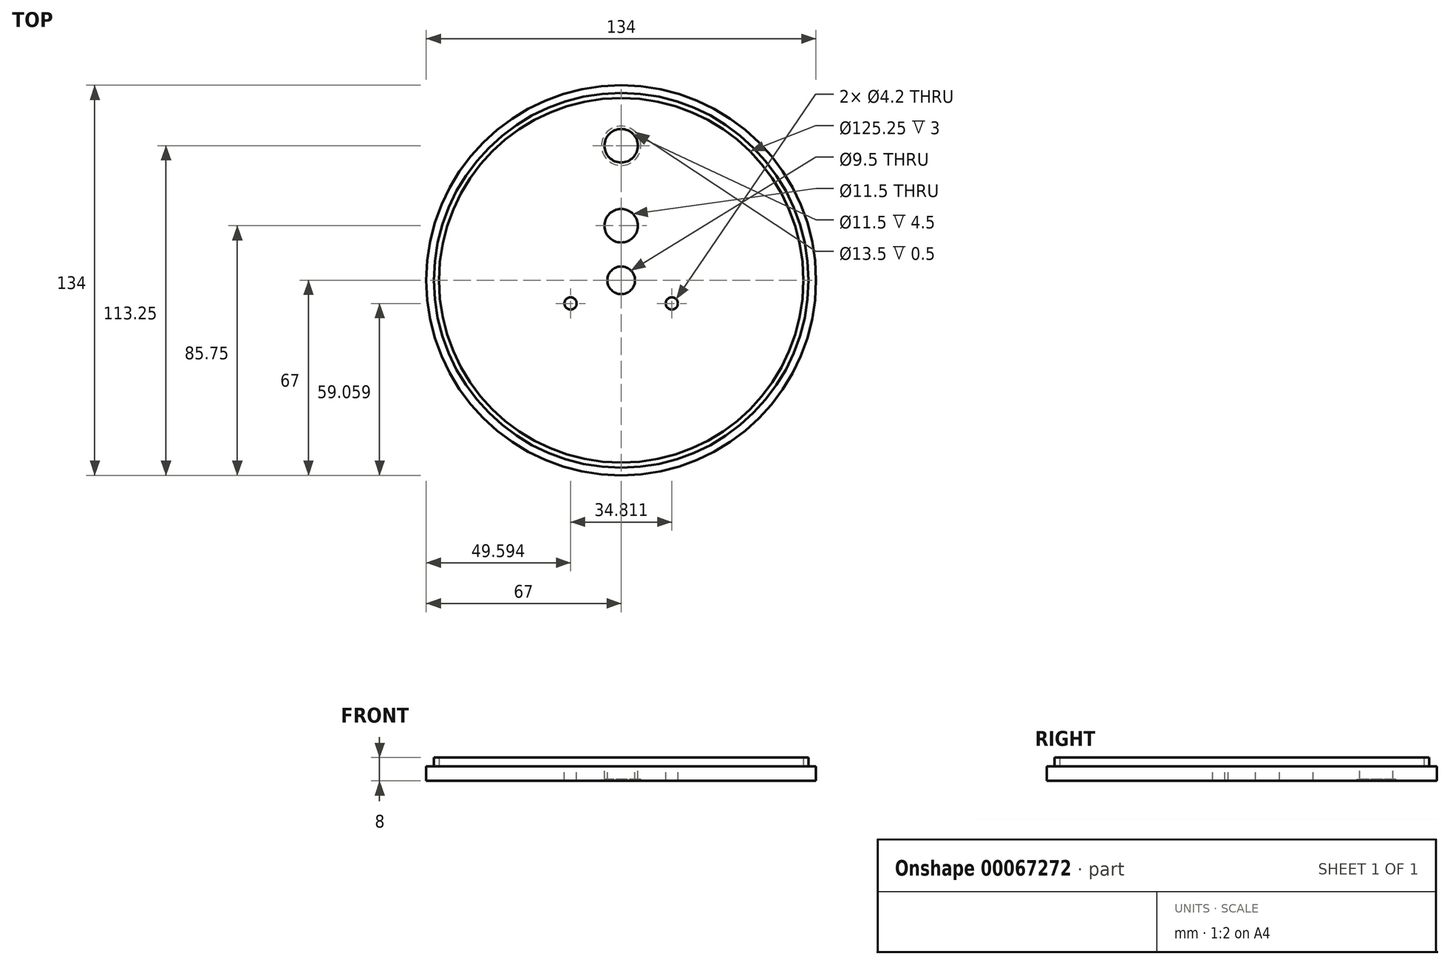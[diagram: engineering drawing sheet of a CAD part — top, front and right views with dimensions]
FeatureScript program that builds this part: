
annotation { "Feature Type Name" : "Feature", "Feature Type Description" : "" }
export const myFeature = defineFeature(function(context is Context, id is Id, definition is map)
    precondition{}
    {
        {
            var Q0;
            Q0=qCreatedBy(makeId("Top.planeOp"),FACE);
            var sketch = newSketch(context, id + "F0", { "sketchPlane" : qUnion([Q0])});
            skCircle(sketch, "E0", {"center": v(0, 0) * mm, "radius": 67 * mm});
            skSolve(sketch);
        }
        {
            var Q0;
            Q0=makeQuery(id+"F0.imprint","IMPRINT",FACE,{"disambiguationData":[TD([[makeQuery(id+"F0.imprint","IMPRINT",EDGE,{"derivedFrom":sQuery(id+"F0.wireOp",EDGE,"E0")}),1.0]])]});
            extrude(context, id + "F1", {"entities" : qUnion([Q0]), "depth" : 5 * mm});
        }
        {
            var Q0;
            Q0=makeQuery(id+"F1.opExtrude","CAP_FACE",FACE,{"disambiguationData":[OSD([sQuery(id+"F0.wireOp",EDGE,"E0")])],"isStart":false});
            var sketch = newSketch(context, id + "F2", { "sketchPlane" : qUnion([Q0])});
            skCircle(sketch, "E1", {"center": v(0, 0) * mm, "radius": 64.38 * mm});
            skSolve(sketch);
        }
        {
            var Q0;
            Q0=makeQuery(id+"F2.imprint","IMPRINT",FACE,{"disambiguationData":[TD([[makeQuery(id+"F2.imprint","IMPRINT",EDGE,{"derivedFrom":sQuery(id+"F2.wireOp",EDGE,"E1")}),1.0]])]});
            var sketch = newSketch(context, id + "F3", { "sketchPlane" : qUnion([Q0])});
            skCircle(sketch, "E2", {"center": v(0, 0) * mm, "radius": 62.62 * mm});
            skSolve(sketch);
        }
        {
            var Q0;
            Q0=makeQuery(id+"F2.imprint","IMPRINT",FACE,{"disambiguationData":[TD([[makeQuery(id+"F2.imprint","IMPRINT",EDGE,{"derivedFrom":sQuery(id+"F2.wireOp",EDGE,"E1")}),1.0]])]});
            var sketch = newSketch(context, id + "F4", { "sketchPlane" : qUnion([Q0])});
            skCircle(sketch, "E3", {"center": v(0, 0) * mm, "radius": 58.88 * mm});
            skSolve(sketch);
        }
        {
            var Q0;
            Q0=makeQuery(id+"F3.imprint","IMPRINT",FACE,{"disambiguationData":[TD([[makeQuery(id+"F3.imprint","IMPRINT",EDGE,{"derivedFrom":sQuery(id+"F3.wireOp",EDGE,"E2")}),-1.0]])]});
            var Q1;
            Q1=sQuery(id+"F2.wireOp",EDGE,"E1");
            var Q2;
            Q2=sQuery(id+"F3.wireOp",EDGE,"E2");
            extrude(context, id + "F5", {"entities" : qUnion([Q0]), "operationType" : NewBodyOperationType.ADD, "surfaceEntities" : qUnion([Q1, Q2]), "depth" : 3 * mm});
        }
        {
            var Q0;
            Q0=makeQuery(id+"F4.imprint","IMPRINT",FACE,{"disambiguationData":[TD([[makeQuery(id+"F4.imprint","IMPRINT",EDGE,{"derivedFrom":sQuery(id+"F4.wireOp",EDGE,"E3")}),1.0]])]});
            var sketch = newSketch(context, id + "F6", { "sketchPlane" : qUnion([Q0])});
            skCircle(sketch, "E4", {"center": v(0, 0) * mm, "radius": 4.75 * mm});
            skCircle(sketch, "E5", {"center": v(0, 18.75) * mm, "radius": 5.75 * mm});
            skCircle(sketch, "E6", {"center": v(0, 46.25) * mm, "radius": 5.75 * mm});
            skCircle(sketch, "E7.0", {"center": v(0, 18.75) * mm, "radius": 6.75 * mm});
            skCircle(sketch, "E8.0", {"center": v(0, 0) * mm, "radius": 63.88 * mm});
            skCircle(sketch, "E9.0", {"center": v(0, 0) * mm, "radius": 5.75 * mm});
            skCircle(sketch, "E10.0", {"center": v(0, 46.25) * mm, "radius": 6.75 * mm});
            skSolve(sketch);
        }
        {
            var Q0;
            Q0=makeQuery(id+"F6.imprint","IMPRINT",FACE,{"disambiguationData":[TD([[makeQuery(id+"F6.imprint","IMPRINT",EDGE,{"derivedFrom":sQuery(id+"F6.wireOp",EDGE,"E4")}),-1.0]])]});
            var sketch = newSketch(context, id + "F7", { "sketchPlane" : qUnion([Q0])});
            skCircle(sketch, "E11", {"center": v(17.4, -7.94) * mm, "radius": 2.1 * mm});
            skCircle(sketch, "E12.MirrorC", {"center": v(-17.4, -7.94) * mm, "radius": 2.1 * mm});
            skSolve(sketch);
        }
        {
            var Q0;
            Q0 = qSketchRegion(id + "F7", true);
            extrude(context, id + "F8", {"entities" : qUnion([Q0]), "operationType" : NewBodyOperationType.REMOVE, "endBound" : BoundingType.THROUGH_ALL, "oppositeDirection" : true, "depth" : 25 * mm});
        }
        {
            var Q0;
            Q0=makeQuery(id+"F6.imprint","IMPRINT",FACE,{"disambiguationData":[TD([[makeQuery(id+"F6.imprint","IMPRINT",EDGE,{"derivedFrom":sQuery(id+"F6.wireOp",EDGE,"E6")}),1.0]])]});
            var Q1;
            Q1=makeQuery(id+"F6.imprint","IMPRINT",FACE,{"disambiguationData":[TD([[makeQuery(id+"F6.imprint","IMPRINT",EDGE,{"derivedFrom":sQuery(id+"F6.wireOp",EDGE,"E5")}),1.0]])]});
            var Q2;
            Q2=makeQuery(id+"F6.imprint","IMPRINT",FACE,{"disambiguationData":[TD([[makeQuery(id+"F6.imprint","IMPRINT",EDGE,{"derivedFrom":sQuery(id+"F6.wireOp",EDGE,"E4")}),1.0]])]});
            var Q3;
            Q3=sQuery(id+"F6.wireOp",EDGE,"E6");
            extrude(context, id + "F9", {"entities" : qUnion([Q0, Q1, Q2]), "operationType" : NewBodyOperationType.REMOVE, "surfaceEntities" : qUnion([Q3]), "endBound" : BoundingType.THROUGH_ALL, "oppositeDirection" : true, "depth" : 25 * mm});
        }
        {
            var Q0;
            Q0=qCreatedBy(makeId("Top.planeOp"),FACE);
            var sketch = newSketch(context, id + "F10", { "sketchPlane" : qUnion([Q0])});
            skCircle(sketch, "E13.0", {"center": v(0, 46.25) * mm, "radius": 6.75 * mm});
            skCircle(sketch, "E14.0", {"center": v(0, 0) * mm, "radius": 63.88 * mm});
            skCircle(sketch, "E15.0", {"center": v(0, 18.75) * mm, "radius": 6.75 * mm});
            skCircle(sketch, "E16.0", {"center": v(0, 0) * mm, "radius": 5.75 * mm});
            skSolve(sketch);
        }
        {
            var Q0;
            Q0=makeQuery(id+"F10.imprint","IMPRINT",FACE,{"disambiguationData":[TD([[makeQuery(id+"F10.imprint","IMPRINT",EDGE,{"derivedFrom":sQuery(id+"F10.wireOp",EDGE,"E13.0")}),1.0]])]});
            var Q1;
            Q1=makeQuery(id+"F10.imprint","IMPRINT",FACE,{"disambiguationData":[TD([[makeQuery(id+"F10.imprint","IMPRINT",EDGE,{"derivedFrom":sQuery(id+"F10.wireOp",EDGE,"E15.0")}),1.0]])]});
            var Q2;
            Q2=makeQuery(id+"F10.imprint","IMPRINT",FACE,{"disambiguationData":[TD([[makeQuery(id+"F10.imprint","IMPRINT",EDGE,{"derivedFrom":sQuery(id+"F10.wireOp",EDGE,"E16.0")}),1.0]])]});
            extrude(context, id + "F11", {"entities" : qUnion([Q0, Q1, Q2]), "operationType" : NewBodyOperationType.REMOVE, "oppositeDirection" : true, "depth" : 0.5 * mm});
        }
        {
            var Q0;
            Q0=makeQuery(id+"F10.imprint","IMPRINT",FACE,{"disambiguationData":[TD([[makeQuery(id+"F10.imprint","IMPRINT",EDGE,{"derivedFrom":sQuery(id+"F10.wireOp",EDGE,"E13.0")}),1.0]])]});
            extrude(context, id + "F12", {"entities" : qUnion([Q0]), "operationType" : NewBodyOperationType.REMOVE, "depth" : 0.5 * mm});
        }
    });
